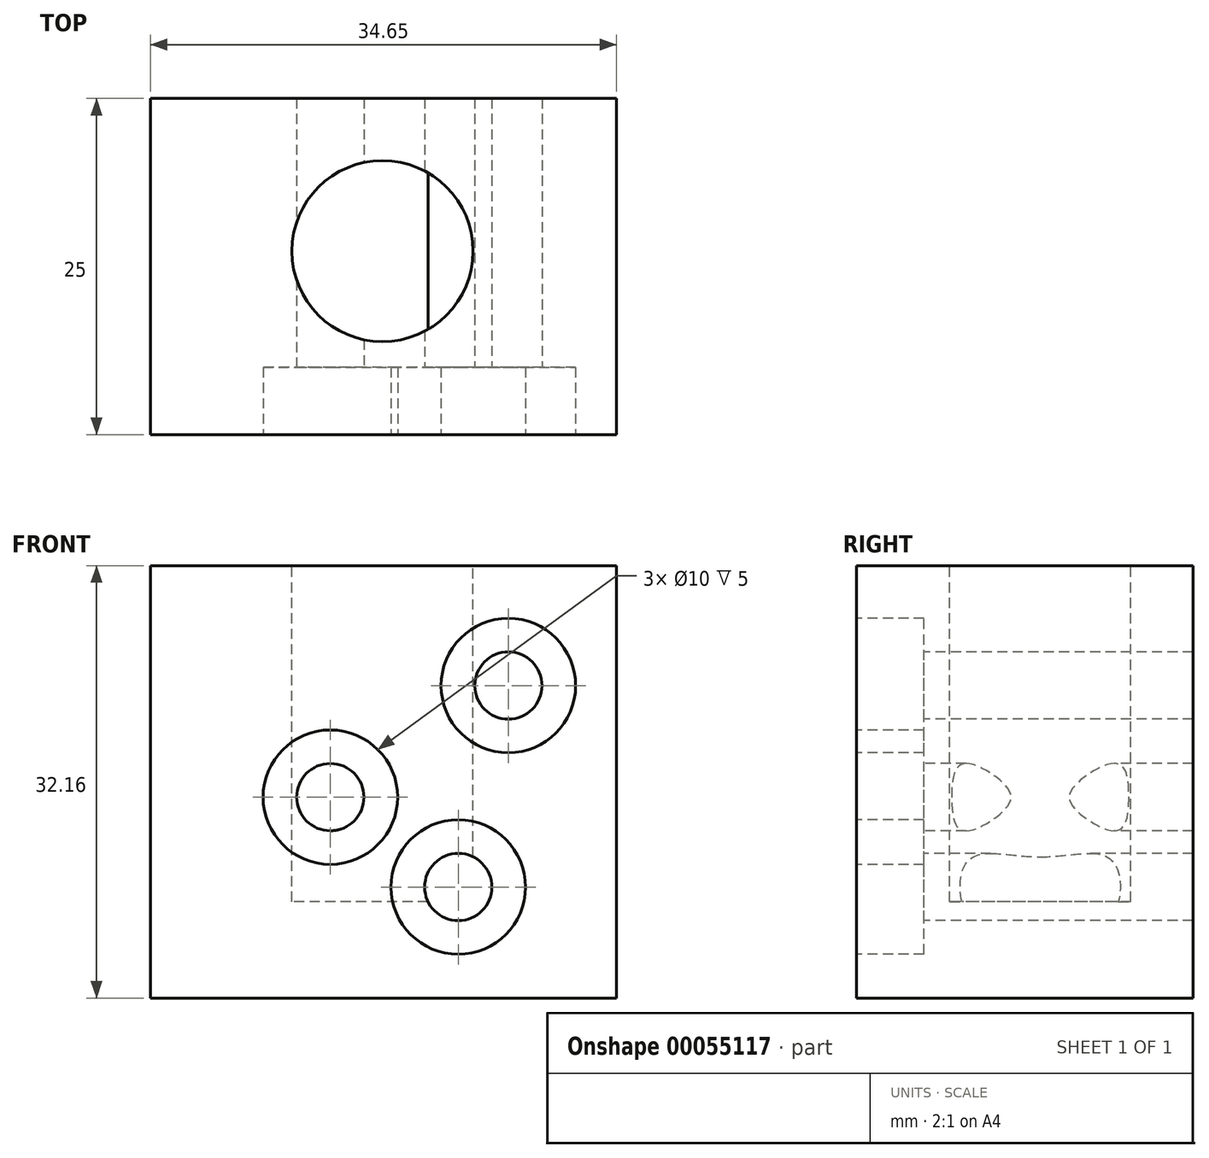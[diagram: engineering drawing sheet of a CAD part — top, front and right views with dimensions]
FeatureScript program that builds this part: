
annotation { "Feature Type Name" : "Feature", "Feature Type Description" : "" }
export const myFeature = defineFeature(function(context is Context, id is Id, definition is map)
    precondition{}
    {
        {
            var Q0;
            Q0=qCreatedBy(makeId("Front.planeOp"),FACE);
            var sketch = newSketch(context, id + "F0", { "sketchPlane" : qUnion([Q0])});
            skLineSegment(sketch, "E0.bottom", {"start": v(0, 0) * mm, "end": v(34.65, 0) * mm});
            skLineSegment(sketch, "E0.top", {"start": v(0, 32.16) * mm, "end": v(34.65, 32.16) * mm});
            skLineSegment(sketch, "E0.left", {"start": v(0, 0) * mm, "end": v(0, 32.16) * mm});
            skLineSegment(sketch, "E0.right", {"start": v(34.65, 0) * mm, "end": v(34.65, 32.16) * mm});
            skSolve(sketch);
        }
        {
            var Q0;
            Q0 = qSketchRegion(id + "F0", true);
            extrude(context, id + "F1", {"entities" : qUnion([Q0]), "depth" : 25 * mm});
        }
        {
            var Q0;
            Q0=makeQuery(id+"F1.opExtrude","SWEPT_FACE",FACE,{"disambiguationData":[OSD([sQuery(id+"F0.wireOp",EDGE,"E0.top")])]});
            var sketch = newSketch(context, id + "F2", { "sketchPlane" : qUnion([Q0])});
            skCircle(sketch, "E1", {"center": v(17.26, -11.36) * mm, "radius": 6.73 * mm});
            skSolve(sketch);
        }
        {
            var Q0;
            Q0 = qSketchRegion(id + "F2", true);
            extrude(context, id + "F3", {"entities" : qUnion([Q0]), "operationType" : NewBodyOperationType.REMOVE, "oppositeDirection" : true, "depth" : 25 * mm});
        }
        {
            var Q0;
            Q0=makeQuery(id+"F1.opExtrude","CAP_FACE",FACE,{"disambiguationData":[OSD([sQuery(id+"F0.wireOp",EDGE,"E0.bottom"),sQuery(id+"F0.wireOp",EDGE,"E0.top"),sQuery(id+"F0.wireOp",EDGE,"E0.left"),sQuery(id+"F0.wireOp",EDGE,"E0.right")])],"isStart":false});
            var sketch = newSketch(context, id + "F4", { "sketchPlane" : qUnion([Q0])});
            skPoint(sketch, "E2", {"position": v(13.38, 14.94) * mm});
            skPoint(sketch, "E3", {"position": v(26.62, 23.24) * mm});
            skPoint(sketch, "E4", {"position": v(22.9, 8.25) * mm});
            skSolve(sketch);
        }
        {
            var Q0;
            Q0=sQuery(id+"F4.wireOp",VERTEX,"E2");
            var Q1;
            Q1=sQuery(id+"F4.wireOp",VERTEX,"E3");
            var Q2;
            Q2=sQuery(id+"F4.wireOp",VERTEX,"E4");
            var Q3;
            Q3=makeQuery(id+"F1.opExtrude","SWEPT_BODY",BODY,{"disambiguationData":[OSD([sQuery(id+"F0.wireOp",EDGE,"E0.bottom"),sQuery(id+"F0.wireOp",EDGE,"E0.top"),sQuery(id+"F0.wireOp",EDGE,"E0.left"),sQuery(id+"F0.wireOp",EDGE,"E0.right")])]});
            hole(context, id + "F5", {"style" : HoleStyle.C_BORE, "holeDiameter" : 5 * mm, "cBoreDiameter" : 10 * mm, "cBoreDepth" : 5 * mm, "endStyle" : HoleEndStyle.THROUGH, "locations" : qUnion([Q0, Q1, Q2]), "scope" : qUnion([Q3])});
        }
    });
